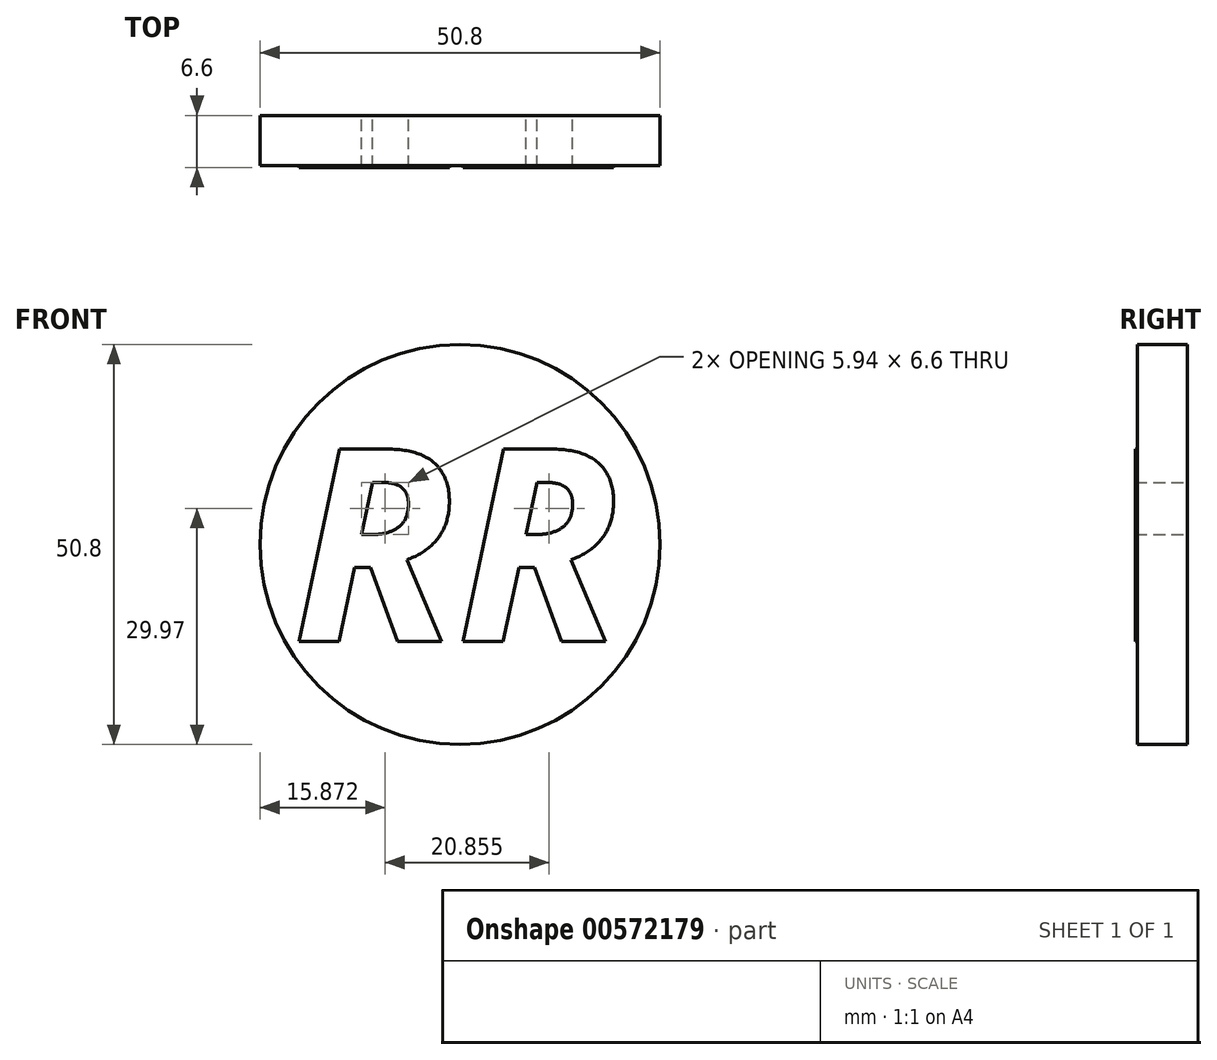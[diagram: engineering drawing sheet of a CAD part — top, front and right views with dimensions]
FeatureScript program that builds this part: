
annotation { "Feature Type Name" : "Feature", "Feature Type Description" : "" }
export const myFeature = defineFeature(function(context is Context, id is Id, definition is map)
    precondition{}
    {
        {
            var Q0;
            Q0=qCreatedBy(makeId("Front.planeOp"),FACE);
            var sketch = newSketch(context, id + "F0", { "sketchPlane" : qUnion([Q0])});
            skCircle(sketch, "E0", {"center": v(0, 0) * mm, "radius": 25.4 * mm});
            skText(sketch, "E1", { "text": "RR", "fontName": "OpenSans-BoldItalic.ttf"});
            skCircle(sketch, "E2.0", {"center": v(0, 0) * mm, "radius": 27.94 * mm});
            const initialGuessF0  = {"E1": [-0.02136, -0.01233, 1, 0, 0.02466]};
            skSetInitialGuess(sketch, initialGuessF0);
            skSolve(sketch);
        }
        {
            var Q0;
            Q0=makeQuery(id+"F0.imprint","IMPRINT",FACE,{"disambiguationData":[TD([[makeQuery(id+"F0.imprint","IMPRINT",EDGE,{"derivedFrom":sQuery(id+"F0.wireOp",EDGE,"E0")}),1.0]])]});
            extrude(context, id + "F1", {"entities" : qUnion([Q0]), "depth" : 6.35 * mm, "offsetDistance" : 25.4 * mm});
        }
        {
            var Q0;
            Q0=sQuery(id+"F0.wireOp",EDGE,"E0");
            var Q1;
            Q1=sQuery(id+"F0.wireOp",EDGE,"E2.0");
            extrude(context, id + "F2", {"bodyType" : ToolBodyType.SURFACE, "surfaceEntities" : qUnion([Q0, Q1]), "depth" : 584.2 * mm, "offsetDistance" : 25.4 * mm});
        }
        {
            var Q0;
            Q0=makeQuery(id+"F0.imprint","IMPRINT",FACE,{"disambiguationData":[TD([[makeQuery(id+"F0.imprint","IMPRINT",EDGE,{"derivedFrom":sQuery(id+"F0.wireOp",EDGE,"E1.sketch_text.stroke-19")}),-1.0]])]});
            extrude(context, id + "F3", {"entities" : qUnion([Q0]), "operationType" : NewBodyOperationType.ADD, "depth" : 6.6 * mm, "offsetDistance" : 25.4 * mm});
        }
        {
            var Q0;
            Q0=makeQuery(id+"F0.imprint","IMPRINT",FACE,{"disambiguationData":[TD([[makeQuery(id+"F0.imprint","IMPRINT",EDGE,{"derivedFrom":sQuery(id+"F0.wireOp",EDGE,"E1.sketch_text.stroke-0")}),-1.0]])]});
            extrude(context, id + "F4", {"entities" : qUnion([Q0]), "operationType" : NewBodyOperationType.ADD, "depth" : 6.6 * mm, "offsetDistance" : 25.4 * mm});
        }
    });
